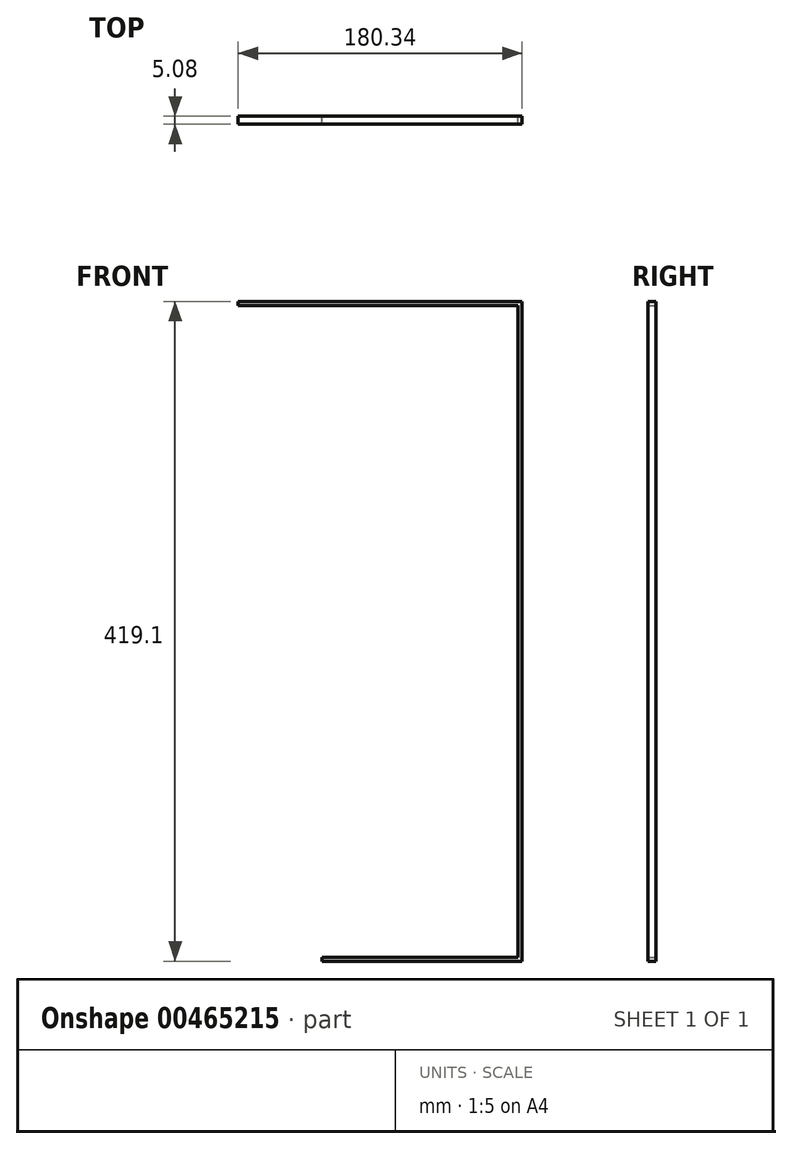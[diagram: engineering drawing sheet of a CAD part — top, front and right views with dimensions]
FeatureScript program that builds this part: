
annotation { "Feature Type Name" : "Feature", "Feature Type Description" : "" }
export const myFeature = defineFeature(function(context is Context, id is Id, definition is map)
    precondition{}
    {
        {
            var Q0;
            Q0=qCreatedBy(makeId("Front.planeOp"),FACE);
            var sketch = newSketch(context, id + "F0", { "sketchPlane" : qUnion([Q0])});
            skLineSegment(sketch, "E0.bottom", {"start": v(0, 0) * mm, "end": v(127, 0) * mm});
            skLineSegment(sketch, "E0.top", {"start": v(0, 2.54) * mm, "end": v(127, 2.54) * mm});
            skLineSegment(sketch, "E0.left", {"start": v(0, 0) * mm, "end": v(0, 2.54) * mm});
            skLineSegment(sketch, "E0.right", {"start": v(127, 0) * mm, "end": v(127, 2.54) * mm});
            skLineSegment(sketch, "E1.bottom", {"start": v(124.46, 0) * mm, "end": v(127, 0) * mm});
            skLineSegment(sketch, "E1.top", {"start": v(124.46, 416.56) * mm, "end": v(127, 416.56) * mm});
            skLineSegment(sketch, "E1.left", {"start": v(127, 0) * mm, "end": v(127, 416.56) * mm});
            skLineSegment(sketch, "E1.right", {"start": v(124.46, 0) * mm, "end": v(124.46, 416.56) * mm});
            skLineSegment(sketch, "E2.right", {"start": v(0, 39.92) * mm, "end": v(0, 42.5) * mm});
            skLineSegment(sketch, "E3.bottom", {"start": v(127, 416.56) * mm, "end": v(-53.34, 416.56) * mm});
            skLineSegment(sketch, "E3.top", {"start": v(127, 419.1) * mm, "end": v(-53.34, 419.1) * mm});
            skLineSegment(sketch, "E3.left", {"start": v(127, 416.56) * mm, "end": v(127, 419.1) * mm});
            skLineSegment(sketch, "E3.right", {"start": v(-53.34, 416.56) * mm, "end": v(-53.34, 419.1) * mm});
            skSolve(sketch);
        }
        {
            var Q0;
            Q0 = qSketchRegion(id + "F0", true);
            extrude(context, id + "F1", {"entities" : qUnion([Q0]), "depth" : 5.08 * mm});
        }
    });
